# Revit family: DTI_A3-BSQTZMSOHS
name_source: partatom
category: Doors
revit_build: Autodesk Revit 2016 (Build: 20150220_1215(x64)
units: mm (PartAtom-declared; Revit-internal decimal feet)

## family parameters
Always vertical = Yes
Cut with Voids When Loaded = No
Host = Wall
OmniClass Number = 23.30.10.00
OmniClass Title = Doors
Room Calculation Point = No
Shared = No

## types (1)
- BSQTZMSOHS
    Cill Height = 50 mm  [stored 0.164042 ft]
    Description = Quartz Half Security BSQTZMSOHS
    Door Frame Material = Meranti
    Door Height = 2032 mm
    Door Material = Meranti
    Door Width = 813 mm
    Frame Depth = 70 mm  [stored 0.229659 ft]
    Frame Width = 70 mm  [stored 0.229659 ft]
    Function = Exterior
    Height = 2052 mm  [stored 6.73228 ft]
    Manufacturer = Swartland Doors & Windows
    Model = BSQTZMSOHS
    Rough Height = 2165 mm
    Rough Width = 923 mm
    URL = www.swartland.co.za
    Wall Closure = By host
    Width = 953 mm

note: [stored X ft] marks values corroborated as IEEE doubles in the binary element streams (Revit-internal decimal feet)

## geometry (parser evidence)
native form markers: Blend x6, Sweep x5
no freeform markers — native parametric forms only
